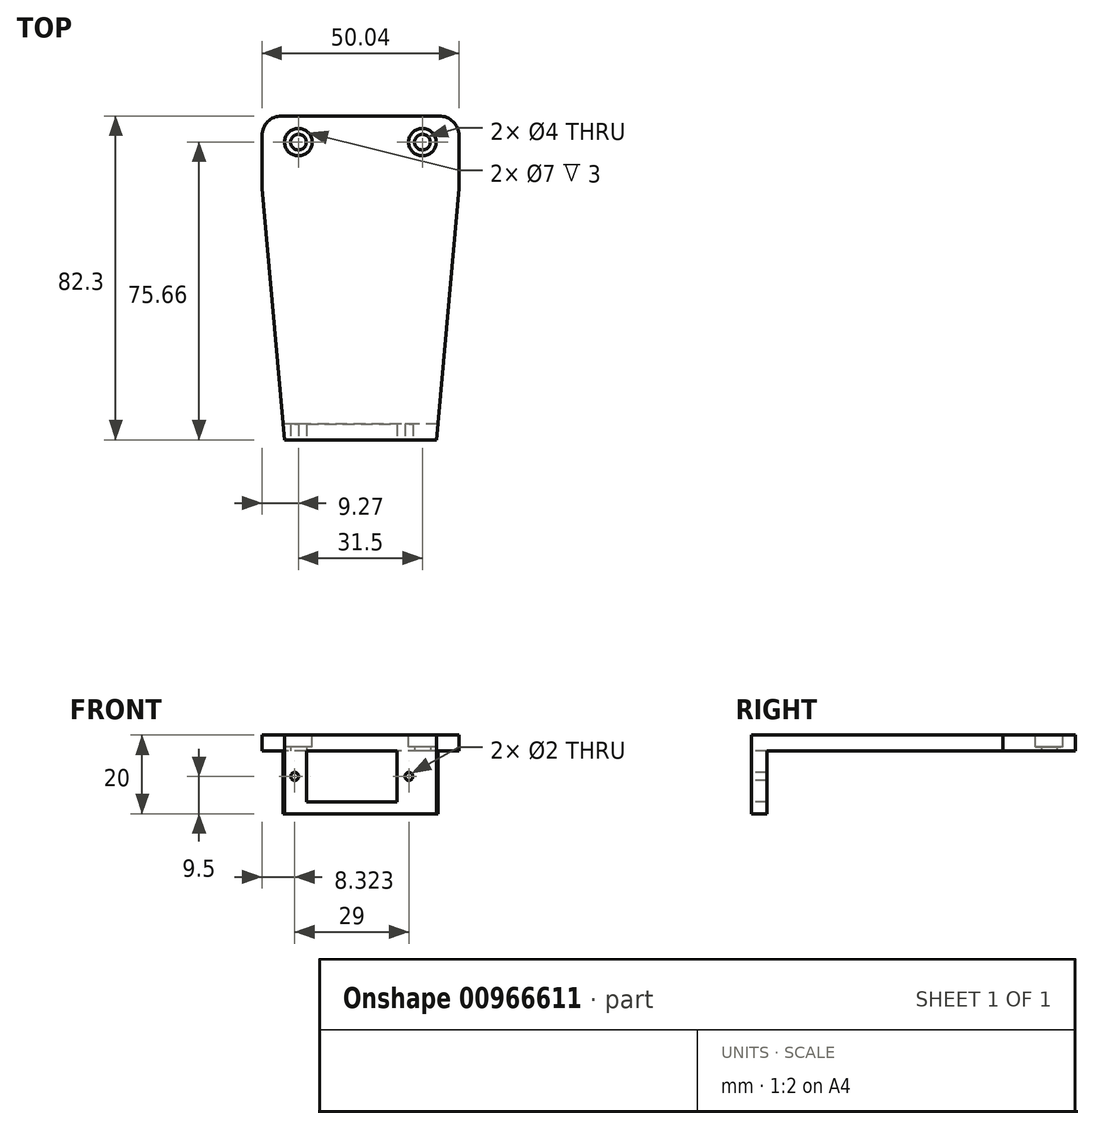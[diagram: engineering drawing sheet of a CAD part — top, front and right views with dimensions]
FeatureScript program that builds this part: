
annotation { "Feature Type Name" : "Feature", "Feature Type Description" : "" }
export const myFeature = defineFeature(function(context is Context, id is Id, definition is map)
    precondition{}
    {
        {
            var Q0;
            Q0=qCreatedBy(makeId("Top.planeOp"),FACE);
            var sketch = newSketch(context, id + "F0", { "sketchPlane" : qUnion([Q0])});
            skLineSegment(sketch, "E0", {"start": v(-25.02, 6.64) * mm, "end": v(-25.02, -11.78) * mm});
            skLineSegment(sketch, "E1", {"start": v(-25.02, -11.78) * mm, "end": v(-19.3, -75.66) * mm});
            skLineSegment(sketch, "E2", {"start": v(-19.3, -75.66) * mm, "end": v(0, -75.66) * mm});
            skLineSegment(sketch, "E3", {"start": v(-25.02, 6.64) * mm, "end": v(0, 6.64) * mm});
            skCircle(sketch, "E4", {"center": v(-15.75, 0) * mm, "radius": 2 * mm});
            skLineSegment(sketch, "E5.MirrorCS", {"start": v(25.02, -11.78) * mm, "end": v(19.3, -75.66) * mm});
            skLineSegment(sketch, "E6.MirrorCS", {"start": v(19.3, -75.66) * mm, "end": v(0, -75.66) * mm});
            skLineSegment(sketch, "E7.MirrorCS", {"start": v(25.02, 6.64) * mm, "end": v(25.02, -11.78) * mm});
            skCircle(sketch, "E8.MirrorC", {"center": v(15.75, 0) * mm, "radius": 2 * mm});
            skLineSegment(sketch, "E9.MirrorCS", {"start": v(25.02, 6.64) * mm, "end": v(0, 6.64) * mm});
            skSolve(sketch);
        }
        {
            var Q0;
            Q0 = qSketchRegion(id + "F0", true);
            extrude(context, id + "F1", {"entities" : qUnion([Q0]), "depth" : 4 * mm, "offsetDistance" : 25 * mm});
        }
        {
            var Q0;
            Q0=makeQuery(id+"F1.opExtrude","CAP_FACE",FACE,{"disambiguationData":[OSD([sQuery(id+"F0.wireOp",EDGE,"E0"),sQuery(id+"F0.wireOp",EDGE,"E1"),sQuery(id+"F0.wireOp",EDGE,"E2"),sQuery(id+"F0.wireOp",EDGE,"E3"),sQuery(id+"F0.wireOp",EDGE,"E4"),sQuery(id+"F0.wireOp",EDGE,"lEilLTsY-392m-Hhmt-hR3z-KQXnIn7UWD5q"),sQuery(id+"F0.wireOp",EDGE,"p8SVaZev-5UtS-8D91-98Vv-zzmttBRP2PUu"),sQuery(id+"F0.wireOp",EDGE,"O0eZJeTP-dGfr-gXZP-p64k-3EXRJ4vv6RCz"),sQuery(id+"F0.wireOp",EDGE,"bebf61c4-f442-4e3f-ab49-61e7f98a418c0.MirrorC"),sQuery(id+"F0.wireOp",EDGE,"E5.MirrorCS"),sQuery(id+"F0.wireOp",EDGE,"E6.MirrorCS"),sQuery(id+"F0.wireOp",EDGE,"E7.MirrorCS"),sQuery(id+"F0.wireOp",EDGE,"E8.MirrorC"),sQuery(id+"F0.wireOp",EDGE,"E9.MirrorCS"),sQuery(id+"F0.wireOp",EDGE,"372EEgm9-B3gC-qM5e-1NJW-E4PBRk3e4eMb"),sQuery(id+"F0.wireOp",EDGE,"epesgIHb-o9eh-k72Z-hkFH-KvsoaFuctqg3"),sQuery(id+"F0.wireOp",EDGE,"QsPb3Uh4-4dlv-2tyk-5NrK-SBb10c5aRr1p"),sQuery(id+"F0.wireOp",EDGE,"649c4b4f-d164-4939-ba4c-a0c5b6812db80.MirrorCS"),sQuery(id+"F0.wireOp",EDGE,"f6046833-8c1d-4d61-bf68-2d72a587ff670.MirrorCS"),sQuery(id+"F0.wireOp",EDGE,"50d17d0e-e000-42ef-947d-4fd535aea2370.MirrorCS")])],"isStart":false});
            var sketch = newSketch(context, id + "F2", { "sketchPlane" : qUnion([Q0])});
            skCircle(sketch, "E10", {"center": v(-15.75, 0) * mm, "radius": 3.5 * mm});
            skCircle(sketch, "E11.MirrorC", {"center": v(15.75, 0) * mm, "radius": 3.5 * mm});
            skSolve(sketch);
        }
        {
            var Q0;
            Q0 = qSketchRegion(id + "F2", true);
            extrude(context, id + "F3", {"entities" : qUnion([Q0]), "operationType" : NewBodyOperationType.REMOVE, "oppositeDirection" : true, "depth" : 3 * mm, "offsetDistance" : 25 * mm});
        }
        {
            var Q0;
            Q0=makeQuery(id+"F1.opExtrude","CAP_FACE",FACE,{"disambiguationData":[OSD([sQuery(id+"F0.wireOp",EDGE,"E0"),sQuery(id+"F0.wireOp",EDGE,"E1"),sQuery(id+"F0.wireOp",EDGE,"E2"),sQuery(id+"F0.wireOp",EDGE,"E3"),sQuery(id+"F0.wireOp",EDGE,"E4"),sQuery(id+"F0.wireOp",EDGE,"E5.MirrorCS"),sQuery(id+"F0.wireOp",EDGE,"E6.MirrorCS"),sQuery(id+"F0.wireOp",EDGE,"E7.MirrorCS"),sQuery(id+"F0.wireOp",EDGE,"E8.MirrorC"),sQuery(id+"F0.wireOp",EDGE,"E9.MirrorCS")])],"isStart":true});
            var sketch = newSketch(context, id + "F4", { "sketchPlane" : qUnion([Q0])});
            skLineSegment(sketch, "E12.bottom", {"start": v(-19.3, 75.66) * mm, "end": v(19.3, 75.66) * mm});
            skLineSegment(sketch, "E13", {"start": v(19.66, 71.66) * mm, "end": v(19.3, 75.66) * mm});
            skPoint(sketch, "E14.orphan", {"position": v(19.5, 75.66) * mm});
            skLineSegment(sketch, "E15", {"start": v(19.66, 71.66) * mm, "end": v(-19.66, 71.66) * mm});
            skLineSegment(sketch, "E16", {"start": v(-19.3, 75.66) * mm, "end": v(-19.66, 71.66) * mm});
            skSolve(sketch);
        }
        {
            var Q0;
            Q0 = qSketchRegion(id + "F4", true);
            extrude(context, id + "F5", {"entities" : qUnion([Q0]), "operationType" : NewBodyOperationType.ADD, "depth" : 16 * mm, "offsetDistance" : 25 * mm});
        }
        {
            var Q0;
            Q0=makeQuery(id+"F5.boolean.opBoolean","MERGE",FACE,{"derivedFrom":[makeQuery(id+"F1.opExtrude","SWEPT_FACE",FACE,{"disambiguationData":[OSD([sQuery(id+"F0.wireOp",EDGE,"E2"),sQuery(id+"F0.wireOp",EDGE,"E6.MirrorCS")])]}),makeQuery(id+"F5.opExtrude","SWEPT_FACE",FACE,{"disambiguationData":[OSD([sQuery(id+"F4.wireOp",EDGE,"E12.bottom")])]})]});
            var sketch = newSketch(context, id + "F6", { "sketchPlane" : qUnion([Q0])});
            skLineSegment(sketch, "E17.bottom", {"start": v(9.3, 0) * mm, "end": v(-13.7, 0) * mm});
            skLineSegment(sketch, "E17.top", {"start": v(9.3, -13) * mm, "end": v(-13.7, -13) * mm});
            skLineSegment(sketch, "E17.left", {"start": v(9.3, 0) * mm, "end": v(9.3, -13) * mm});
            skLineSegment(sketch, "E17.right", {"start": v(-13.7, 0) * mm, "end": v(-13.7, -13) * mm});
            skLineSegment(sketch, "E18.bottom", {"start": v(-13.7, -13) * mm, "end": v(3.3, -13) * mm});
            skLineSegment(sketch, "E18.top", {"start": v(-13.7, 0) * mm, "end": v(3.3, 0) * mm});
            skLineSegment(sketch, "E18.left", {"start": v(-13.7, -13) * mm, "end": v(-13.7, 0) * mm});
            skLineSegment(sketch, "E18.right", {"start": v(3.3, -13) * mm, "end": v(3.3, 0) * mm});
            skCircle(sketch, "E19", {"center": v(-16.7, -6.5) * mm, "radius": 1 * mm});
            skCircle(sketch, "E20", {"center": v(12.3, -6.5) * mm, "radius": 1 * mm});
            skSolve(sketch);
        }
        {
            var Q0;
            Q0 = qSketchRegion(id + "F6", true);
            extrude(context, id + "F7", {"entities" : qUnion([Q0]), "operationType" : NewBodyOperationType.REMOVE, "oppositeDirection" : true, "depth" : 25 * mm, "offsetDistance" : 25 * mm});
        }
        {
            var Q0;
            Q0=makeQuery(id+"F1.opExtrude","SWEPT_EDGE",EDGE,{"disambiguationData":[OSD([sQuery(id+"F0.wireOp",EDGE,"E7.MirrorCS"),sQuery(id+"F0.wireOp",EDGE,"E9.MirrorCS")])]});
            var Q1;
            Q1=makeQuery(id+"F1.opExtrude","SWEPT_EDGE",EDGE,{"disambiguationData":[OSD([sQuery(id+"F0.wireOp",EDGE,"E0"),sQuery(id+"F0.wireOp",EDGE,"E3")])]});
            fillet(context, id + "F8", {"entities" : qUnion([Q0, Q1]), "radius" : 5 * mm, "tangentPropagation" : true, "allowEdgeOverflow" : false});
        }
    });
